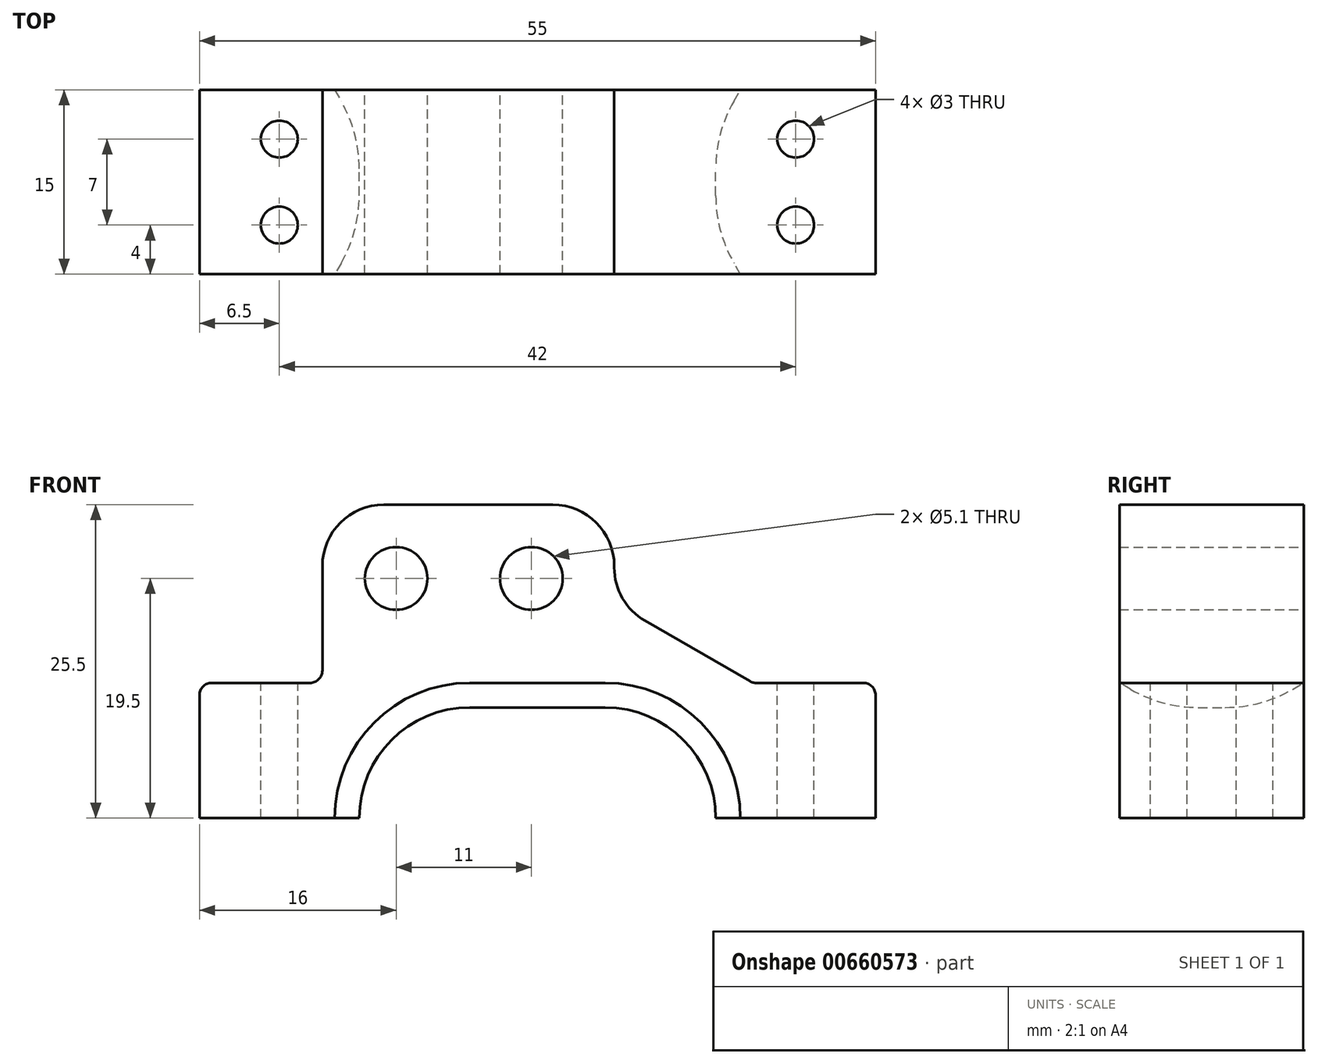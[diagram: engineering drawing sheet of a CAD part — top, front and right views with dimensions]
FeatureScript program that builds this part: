
annotation { "Feature Type Name" : "Feature", "Feature Type Description" : "" }
export const myFeature = defineFeature(function(context is Context, id is Id, definition is map)
    precondition{}
    {
        {
            var Q0;
            Q0=qCreatedBy(makeId("Front.planeOp"),FACE);
            var sketch = newSketch(context, id + "F0", { "sketchPlane" : qUnion([Q0])});
            skArc(sketch, "E0", {"start": v(0, 9) * mm, "mid": v(-9, 0) * mm, "end": v(0, -9) * mm});
            skArc(sketch, "E1", {"start": v(11, -9) * mm, "mid": v(20, 0) * mm, "end": v(11, 9) * mm});
            skLineSegment(sketch, "E2", {"start": v(0, 9) * mm, "end": v(11, 9) * mm});
            skLineSegment(sketch, "E3", {"start": v(0, -9) * mm, "end": v(11, -9) * mm});
            skLineSegment(sketch, "E4", {"start": v(21.52, -9) * mm, "end": v(21.9, -8.8) * mm});
            skPoint(sketch, "E5.orphan", {"position": v(21.52, 9) * mm});
            skCircle(sketch, "E6", {"center": v(-6, 19.5) * mm, "radius": 2.55 * mm});
            skCircle(sketch, "E7", {"center": v(5, 19.5) * mm, "radius": 2.55 * mm});
            skLineSegment(sketch, "E8", {"start": v(-20, 0) * mm, "end": v(-20, 11) * mm});
            skLineSegment(sketch, "E9", {"start": v(-12, 25.5) * mm, "end": v(11.74, 25.5) * mm});
            skLineSegment(sketch, "E10", {"start": v(31, 11) * mm, "end": v(31, -10) * mm});
            skLineSegment(sketch, "E11", {"start": v(23, -15) * mm, "end": v(-12, -15) * mm});
            skLineSegment(sketch, "E12", {"start": v(-20, -15) * mm, "end": v(-20.65, -14.78) * mm});
            skLineSegment(sketch, "E13", {"start": v(-20, -10) * mm, "end": v(-20, 0) * mm});
            skLineSegment(sketch, "E14", {"start": v(-12, 25.5) * mm, "end": v(-12, 11) * mm});
            skLineSegment(sketch, "E15", {"start": v(-12, 11) * mm, "end": v(-20, 11) * mm});
            skLineSegment(sketch, "E16", {"start": v(-20, -10) * mm, "end": v(-12, -10) * mm});
            skLineSegment(sketch, "E17", {"start": v(-12, -10) * mm, "end": v(-12, -15) * mm});
            skLineSegment(sketch, "E18", {"start": v(23, 11) * mm, "end": v(31, 11) * mm});
            skLineSegment(sketch, "E19", {"start": v(31, -10) * mm, "end": v(23, -10) * mm});
            skLineSegment(sketch, "E20", {"start": v(23, -10) * mm, "end": v(23, -15) * mm});
            skPoint(sketch, "E21.orphan", {"position": v(22.74, 25.5) * mm});
            skLineSegment(sketch, "E22", {"start": v(11.74, 25.5) * mm, "end": v(11.74, 17.5) * mm});
            skLineSegment(sketch, "E23", {"start": v(23, 11) * mm, "end": v(11.74, 17.5) * mm});
            skPoint(sketch, "E24.end.orphan", {"position": v(23, 17.5) * mm});
            skSolve(sketch);
        }
        {
            var Q0;
            Q0=makeQuery(id+"F0.imprint","IMPRINT",FACE,{"disambiguationData":[TD([[makeQuery(id+"F0.imprint","IMPRINT",EDGE,{"derivedFrom":sQuery(id+"F0.wireOp",EDGE,"E0")}),-1.0]])]});
            extrude(context, id + "F1", {"entities" : qUnion([Q0]), "depth" : 15 * mm, "offsetDistance" : 25 * mm});
        }
        {
            var Q0;
            Q0=makeQuery(id+"F1.opExtrude","SWEPT_EDGE",EDGE,{"disambiguationData":[OSD([sQuery(id+"F0.wireOp",EDGE,"E9"),sQuery(id+"F0.wireOp",EDGE,"E22")])]});
            var Q1;
            Q1=makeQuery(id+"F1.opExtrude","SWEPT_EDGE",EDGE,{"disambiguationData":[OSD([sQuery(id+"F0.wireOp",EDGE,"E9"),sQuery(id+"F0.wireOp",EDGE,"E14")])]});
            var Q2;
            Q2=makeQuery(id+"F1.opExtrude","SWEPT_EDGE",EDGE,{"disambiguationData":[OSD([sQuery(id+"F0.wireOp",EDGE,"E11"),sQuery(id+"F0.wireOp",EDGE,"E17")])]});
            var Q3;
            Q3=makeQuery(id+"F1.opExtrude","SWEPT_EDGE",EDGE,{"disambiguationData":[OSD([sQuery(id+"F0.wireOp",EDGE,"E11"),sQuery(id+"F0.wireOp",EDGE,"E20")])]});
            var Q4;
            Q4=makeQuery(id+"F1.opExtrude","SWEPT_EDGE",EDGE,{"disambiguationData":[OSD([sQuery(id+"F0.wireOp",EDGE,"E22"),sQuery(id+"F0.wireOp",EDGE,"E23")])]});
            fillet(context, id + "F2", {"entities" : qUnion([Q0, Q1, Q2, Q3, Q4]), "radius" : 5 * mm, "tangentPropagation" : true, "allowEdgeOverflow" : false});
        }
        {
            var Q0;
            Q0=makeQuery(id+"F1.opExtrude","SWEPT_FACE",FACE,{"disambiguationData":[OSD([sQuery(id+"F0.wireOp",EDGE,"E15")])]});
            var sketch = newSketch(context, id + "F3", { "sketchPlane" : qUnion([Q0])});
            skLineSegment(sketch, "E25", {"start": v(-15.5, 0) * mm, "end": v(-15.5, -15) * mm, "construction": true});
            skCircle(sketch, "E26", {"center": v(-15.5, -4) * mm, "radius": 1.5 * mm});
            skCircle(sketch, "E27", {"center": v(-15.5, -11) * mm, "radius": 1.5 * mm});
            skSolve(sketch);
        }
        {
            var Q0;
            Q0=makeQuery(id+"F3.imprint","IMPRINT",FACE,{"disambiguationData":[TD([[makeQuery(id+"F3.imprint","IMPRINT",EDGE,{"derivedFrom":sQuery(id+"F3.wireOp",EDGE,"E26")}),1.0]])]});
            var Q1;
            Q1=makeQuery(id+"F3.imprint","IMPRINT",FACE,{"disambiguationData":[TD([[makeQuery(id+"F3.imprint","IMPRINT",EDGE,{"derivedFrom":sQuery(id+"F3.wireOp",EDGE,"E27")}),1.0]])]});
            extrude(context, id + "F4", {"entities" : qUnion([Q0, Q1]), "operationType" : NewBodyOperationType.REMOVE, "oppositeDirection" : true, "depth" : 25 * mm, "offsetDistance" : 25 * mm});
        }
        {
            var Q0;
            Q0=makeQuery(id+"F1.opExtrude","SWEPT_FACE",FACE,{"disambiguationData":[OSD([sQuery(id+"F0.wireOp",EDGE,"E18")])]});
            var sketch = newSketch(context, id + "F5", { "sketchPlane" : qUnion([Q0])});
            skLineSegment(sketch, "E28", {"start": v(26.5, 0) * mm, "end": v(26.5, -15) * mm, "construction": true});
            skCircle(sketch, "E29", {"center": v(26.5, -4) * mm, "radius": 1.5 * mm});
            skCircle(sketch, "E30", {"center": v(26.5, -11) * mm, "radius": 1.5 * mm});
            skSolve(sketch);
        }
        {
            var Q0;
            Q0=makeQuery(id+"F5.imprint","IMPRINT",FACE,{"disambiguationData":[TD([[makeQuery(id+"F5.imprint","IMPRINT",EDGE,{"derivedFrom":sQuery(id+"F5.wireOp",EDGE,"E29")}),1.0]])]});
            var Q1;
            Q1=makeQuery(id+"F5.imprint","IMPRINT",FACE,{"disambiguationData":[TD([[makeQuery(id+"F5.imprint","IMPRINT",EDGE,{"derivedFrom":sQuery(id+"F5.wireOp",EDGE,"E30")}),1.0]])]});
            extrude(context, id + "F6", {"entities" : qUnion([Q0, Q1]), "operationType" : NewBodyOperationType.REMOVE, "oppositeDirection" : true, "depth" : 25 * mm, "offsetDistance" : 25 * mm});
        }
        {
            var Q0;
            Q0=makeQuery(id+"F1.opExtrude","CAP_EDGE",EDGE,{"disambiguationData":[OSD([sQuery(id+"F0.wireOp",EDGE,"E0")])],"isStart":true});
            var Q1;
            Q1=makeQuery(id+"F1.opExtrude","CAP_EDGE",EDGE,{"disambiguationData":[OSD([sQuery(id+"F0.wireOp",EDGE,"E2")])],"isStart":true});
            var Q2;
            Q2=makeQuery(id+"F1.opExtrude","CAP_EDGE",EDGE,{"disambiguationData":[OSD([sQuery(id+"F0.wireOp",EDGE,"E2")])],"isStart":false});
            chamfer(context, id + "F7", {"entities" : qUnion([Q0, Q1, Q2]), "chamferType" : ChamferType.OFFSET_ANGLE, "width" : 2 * mm, "oppositeDirection" : false, "angle" : 60 * degree, "tangentPropagation" : true});
        }
        {
            var Q0;
            {var subQ0=sQuery(id+"F0.wireOp",EDGE,"E0");Q0=makeQuery(id+"F7.opChamfer","BLEND_EDGE",EDGE,{"blendedFrom":[makeQuery(id+"F1.opExtrude","CAP_EDGE",EDGE,{"disambiguationData":[OSD([subQ0])],"isStart":false}),makeQuery(id+"F1.opExtrude","SWEPT_FACE",FACE,{"disambiguationData":[OSD([subQ0])]})],"blendedInto":[makeQuery(id+"F1.opExtrude","SWEPT_FACE",FACE,{"disambiguationData":[OSD([subQ0])]})]});}
            var Q1;
            {var subQ0=sQuery(id+"F0.wireOp",EDGE,"E0");Q1=makeQuery(id+"F7.opChamfer","BLEND_EDGE",EDGE,{"blendedFrom":[makeQuery(id+"F1.opExtrude","CAP_EDGE",EDGE,{"disambiguationData":[OSD([subQ0])],"isStart":true}),makeQuery(id+"F1.opExtrude","SWEPT_FACE",FACE,{"disambiguationData":[OSD([subQ0])]})],"blendedInto":[makeQuery(id+"F1.opExtrude","SWEPT_FACE",FACE,{"disambiguationData":[OSD([subQ0])]})]});}
            fillet(context, id + "F8", {"entities" : qUnion([Q0, Q1]), "radius" : 11 * mm, "tangentPropagation" : true, "allowEdgeOverflow" : false});
        }
        {
            var Q0;
            Q0=makeQuery(id+"F1.opExtrude","SWEPT_EDGE",EDGE,{"disambiguationData":[OSD([sQuery(id+"F0.wireOp",EDGE,"E14"),sQuery(id+"F0.wireOp",EDGE,"E15")])]});
            var Q1;
            Q1=makeQuery(id+"F1.opExtrude","SWEPT_EDGE",EDGE,{"disambiguationData":[OSD([sQuery(id+"F0.wireOp",EDGE,"E18"),sQuery(id+"F0.wireOp",EDGE,"E23")])]});
            var Q2;
            Q2=makeQuery(id+"F2.opFillet","BLEND_EDGE",EDGE,{"blendedFrom":[makeQuery(id+"F1.opExtrude","SWEPT_EDGE",EDGE,{"disambiguationData":[OSD([sQuery(id+"F0.wireOp",EDGE,"E11"),sQuery(id+"F0.wireOp",EDGE,"E20")])]}),makeQuery(id+"F1.opExtrude","SWEPT_FACE",FACE,{"disambiguationData":[OSD([sQuery(id+"F0.wireOp",EDGE,"E19")])]})],"blendedInto":[makeQuery(id+"F1.opExtrude","SWEPT_FACE",FACE,{"disambiguationData":[OSD([sQuery(id+"F0.wireOp",EDGE,"E19")])]})]});
            var Q3;
            Q3=makeQuery(id+"F2.opFillet","BLEND_EDGE",EDGE,{"blendedFrom":[makeQuery(id+"F1.opExtrude","SWEPT_EDGE",EDGE,{"disambiguationData":[OSD([sQuery(id+"F0.wireOp",EDGE,"E11"),sQuery(id+"F0.wireOp",EDGE,"E17")])]}),makeQuery(id+"F1.opExtrude","SWEPT_FACE",FACE,{"disambiguationData":[OSD([sQuery(id+"F0.wireOp",EDGE,"E16")])]})],"blendedInto":[makeQuery(id+"F1.opExtrude","SWEPT_FACE",FACE,{"disambiguationData":[OSD([sQuery(id+"F0.wireOp",EDGE,"E16")])]})]});
            fillet(context, id + "F9", {"entities" : qUnion([Q0, Q1, Q2, Q3]), "radius" : 1 * mm, "tangentPropagation" : true, "allowEdgeOverflow" : false});
        }
        {
            var Q0;
            Q0=qCreatedBy(makeId("Top.planeOp"),FACE);
            var sketch = newSketch(context, id + "F10", { "sketchPlane" : qUnion([Q0])});
            skLineSegment(sketch, "E31.bottom", {"start": v(-34.65, 9.17) * mm, "end": v(41.62, 9.17) * mm});
            skLineSegment(sketch, "E31.top", {"start": v(-34.65, -24.94) * mm, "end": v(41.62, -24.94) * mm});
            skLineSegment(sketch, "E31.left", {"start": v(-34.65, 9.17) * mm, "end": v(-34.65, -24.94) * mm});
            skLineSegment(sketch, "E31.right", {"start": v(41.62, 9.17) * mm, "end": v(41.62, -24.94) * mm});
            skSolve(sketch);
        }
        {
            var Q0;
            Q0=makeQuery(id+"F10.imprint","IMPRINT",FACE,{"disambiguationData":[TD([[makeQuery(id+"F10.imprint","IMPRINT",EDGE,{"derivedFrom":sQuery(id+"F10.wireOp",EDGE,"E31.bottom")}),-1.0]])]});
            extrude(context, id + "F11", {"entities" : qUnion([Q0]), "operationType" : NewBodyOperationType.REMOVE, "oppositeDirection" : true, "depth" : 25 * mm, "offsetDistance" : 25 * mm});
        }
        {
            var Q0;
            Q0=makeQuery(id+"F1.opExtrude","CAP_FACE",FACE,{"disambiguationData":[OSD([sQuery(id+"F0.wireOp",EDGE,"E0"),sQuery(id+"F0.wireOp",EDGE,"E1"),sQuery(id+"F0.wireOp",EDGE,"E2"),sQuery(id+"F0.wireOp",EDGE,"E3"),sQuery(id+"F0.wireOp",EDGE,"E6"),sQuery(id+"F0.wireOp",EDGE,"E7"),sQuery(id+"F0.wireOp",EDGE,"E8"),sQuery(id+"F0.wireOp",EDGE,"E9"),sQuery(id+"F0.wireOp",EDGE,"E10"),sQuery(id+"F0.wireOp",EDGE,"E11"),sQuery(id+"F0.wireOp",EDGE,"E13"),sQuery(id+"F0.wireOp",EDGE,"E14"),sQuery(id+"F0.wireOp",EDGE,"E15"),sQuery(id+"F0.wireOp",EDGE,"E16"),sQuery(id+"F0.wireOp",EDGE,"E17"),sQuery(id+"F0.wireOp",EDGE,"E18"),sQuery(id+"F0.wireOp",EDGE,"E19"),sQuery(id+"F0.wireOp",EDGE,"E20"),sQuery(id+"F0.wireOp",EDGE,"E22"),sQuery(id+"F0.wireOp",EDGE,"E23")])],"isStart":false});
            var sketch = newSketch(context, id + "F12", { "sketchPlane" : qUnion([Q0])});
            skLineSegment(sketch, "E32.bottom", {"start": v(-20, 11) * mm, "end": v(-22, 11) * mm});
            skLineSegment(sketch, "E32.top", {"start": v(-20, 0) * mm, "end": v(-22, 0) * mm});
            skLineSegment(sketch, "E32.left", {"start": v(-20, 11) * mm, "end": v(-20, 0) * mm});
            skLineSegment(sketch, "E32.right", {"start": v(-22, 11) * mm, "end": v(-22, 0) * mm});
            skLineSegment(sketch, "E33.bottom", {"start": v(31, 11) * mm, "end": v(33, 11) * mm});
            skLineSegment(sketch, "E33.top", {"start": v(31, 0) * mm, "end": v(33, 0) * mm});
            skLineSegment(sketch, "E33.left", {"start": v(31, 11) * mm, "end": v(31, 0) * mm});
            skLineSegment(sketch, "E33.right", {"start": v(33, 11) * mm, "end": v(33, 0) * mm});
            skSolve(sketch);
        }
        {
            var Q0;
            Q0=makeQuery(id+"F12.imprint","IMPRINT",FACE,{"disambiguationData":[TD([[makeQuery(id+"F12.imprint","IMPRINT",EDGE,{"derivedFrom":sQuery(id+"F12.wireOp",EDGE,"E32.bottom")}),1.0]])]});
            var Q1;
            Q1=makeQuery(id+"F12.imprint","IMPRINT",FACE,{"disambiguationData":[TD([[makeQuery(id+"F12.imprint","IMPRINT",EDGE,{"derivedFrom":sQuery(id+"F12.wireOp",EDGE,"E33.bottom")}),-1.0]])]});
            extrude(context, id + "F13", {"entities" : qUnion([Q0, Q1]), "operationType" : NewBodyOperationType.ADD, "oppositeDirection" : true, "depth" : 15 * mm, "offsetDistance" : 25 * mm});
        }
        {
            var Q0;
            Q0=makeQuery(id+"F13.opExtrude","SWEPT_EDGE",EDGE,{"disambiguationData":[OSD([sQuery(id+"F12.wireOp",EDGE,"E32.bottom"),sQuery(id+"F12.wireOp",EDGE,"E32.right")])]});
            var Q1;
            Q1=makeQuery(id+"F13.opExtrude","SWEPT_EDGE",EDGE,{"disambiguationData":[OSD([sQuery(id+"F12.wireOp",EDGE,"E33.bottom"),sQuery(id+"F12.wireOp",EDGE,"E33.right")])]});
            fillet(context, id + "F14", {"entities" : qUnion([Q0, Q1]), "radius" : 1 * mm, "tangentPropagation" : true, "allowEdgeOverflow" : false});
        }
    });
